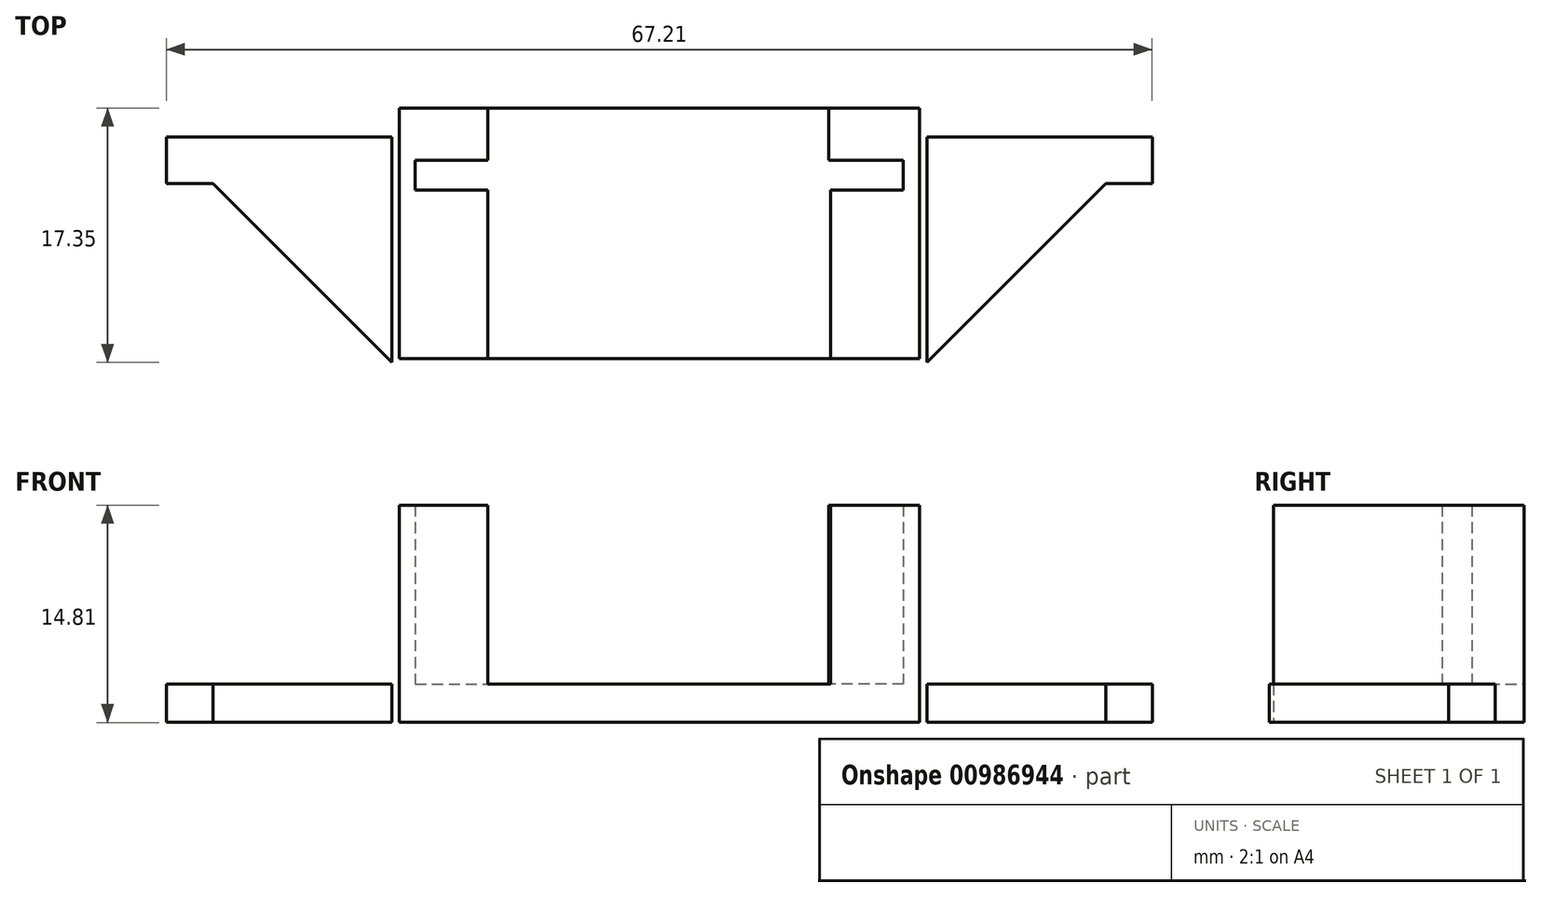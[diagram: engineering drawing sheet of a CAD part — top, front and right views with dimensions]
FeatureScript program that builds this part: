
annotation { "Feature Type Name" : "Feature", "Feature Type Description" : "" }
export const myFeature = defineFeature(function(context is Context, id is Id, definition is map)
    precondition{}
    {
        {
            var Q0;
            Q0=qCreatedBy(makeId("Top.planeOp"),FACE);
            var sketch = newSketch(context, id + "F0", { "sketchPlane" : qUnion([Q0])});
            skLineSegment(sketch, "E0", {"start": v(0, 0) * mm, "end": v(0, -2.03) * mm});
            skLineSegment(sketch, "E1", {"start": v(0, 0) * mm, "end": v(4.57, 0) * mm});
            skLineSegment(sketch, "E2", {"start": v(4.57, 0) * mm, "end": v(4.57, -2.03) * mm});
            skLineSegment(sketch, "E3", {"start": v(0, -2.03) * mm, "end": v(4.57, -2.03) * mm});
            skLineSegment(sketch, "E4.MirrorCS", {"start": v(32.26, -2.03) * mm, "end": v(27.69, -2.03) * mm});
            skLineSegment(sketch, "E5.MirrorCS", {"start": v(32.26, 0) * mm, "end": v(32.26, -2.03) * mm});
            skLineSegment(sketch, "E6.MirrorCS", {"start": v(32.26, 0) * mm, "end": v(27.69, 0) * mm});
            skLineSegment(sketch, "E7.MirrorCS", {"start": v(27.69, 0) * mm, "end": v(27.69, -2.03) * mm});
            skLineSegment(sketch, "E8", {"start": v(-1.6, -1.02) * mm, "end": v(-1.6, 3.56) * mm});
            skLineSegment(sketch, "E9", {"start": v(-1.6, -1.02) * mm, "end": v(-1.6, -5.59) * mm});
            skLineSegment(sketch, "E10", {"start": v(33.86, -1.02) * mm, "end": v(33.86, 3.56) * mm});
            skLineSegment(sketch, "E11", {"start": v(33.86, -1.02) * mm, "end": v(33.86, -5.59) * mm});
            skLineSegment(sketch, "E12.bottom", {"start": v(33.86, -5.59) * mm, "end": v(-1.6, -5.59) * mm});
            skLineSegment(sketch, "E12.top", {"start": v(33.86, 3.56) * mm, "end": v(-1.6, 3.56) * mm});
            skLineSegment(sketch, "E12.left", {"start": v(33.86, -5.59) * mm, "end": v(33.86, 3.56) * mm});
            skLineSegment(sketch, "E12.right", {"start": v(-1.6, -5.59) * mm, "end": v(-1.6, 3.56) * mm});
            skPoint(sketch, "E13.start.orphan", {"position": v(32.26, -1.02) * mm});
            skPoint(sketch, "E14.start.orphan", {"position": v(0, -1.02) * mm});
            skLineSegment(sketch, "E15", {"start": v(4.57, 0) * mm, "end": v(4.57, 3.81) * mm});
            skLineSegment(sketch, "E16", {"start": v(4.57, -2.03) * mm, "end": v(4.57, -9.19) * mm});
            skLineSegment(sketch, "E17", {"start": v(27.69, 0) * mm, "end": v(27.69, 5.45) * mm});
            skLineSegment(sketch, "E18", {"start": v(27.69, 5.45) * mm, "end": v(27.69, -7.68) * mm});
            skSolve(sketch);
        }
        {
            var Q0;
            Q0=makeQuery(id+"F0.imprint","IMPRINT",FACE,{"disambiguationData":[TD([[makeQuery(id+"F0.imprint","IMPRINT",EDGE,{"derivedFrom":sQuery(id+"F0.wireOp",EDGE,"E0")}),-1.0]])]});
            var Q1;
            {var subQ7=sQuery(id+"F0.wireOp",EDGE,"E4.MirrorCS");Q1=makeQuery(id+"F0.imprint","IMPRINT",FACE,{"disambiguationData":[TD([[makeQuery(id+"F0.imprint","IMPRINT",EDGE,{"derivedFrom":subQ7}),1.0]])]});}
            var Q2;
            {var subQ1=sQuery(id+"F0.wireOp",EDGE,"E2");Q2=makeQuery(id+"F0.imprint","IMPRINT",FACE,{"disambiguationData":[TD([[makeQuery(id+"F0.imprint","IMPRINT",EDGE,{"derivedFrom":subQ1}),1.0]])]});}
            var Q3;
            Q3=makeQuery(id+"F0.imprint","IMPRINT",FACE,{"disambiguationData":[TD([[makeQuery(id+"F0.imprint","IMPRINT",EDGE,{"derivedFrom":sQuery(id+"F0.wireOp",EDGE,"E0")}),1.0]])]});
            var Q4;
            {var subQ0=sQuery(id+"F0.wireOp",EDGE,"E4.MirrorCS");Q4=makeQuery(id+"F0.imprint","IMPRINT",FACE,{"disambiguationData":[TD([[makeQuery(id+"F0.imprint","IMPRINT",EDGE,{"derivedFrom":subQ0}),-1.0]])]});}
            extrude(context, id + "F1", {"entities" : qUnion([Q0, Q1, Q2, Q3, Q4]), "depth" : 1.6 * mm, "offsetDistance" : 25.4 * mm});
        }
        {
            var Q0;
            Q0=makeQuery(id+"F1.opExtrude","CAP_FACE",FACE,{"disambiguationData":[OSD([sQuery(id+"F0.wireOp",EDGE,"E12.bottom"),sQuery(id+"F0.wireOp",EDGE,"E12.top"),sQuery(id+"F0.wireOp",EDGE,"E12.left"),sQuery(id+"F0.wireOp",EDGE,"E12.right")])],"isStart":false});
            var sketch = newSketch(context, id + "F2", { "sketchPlane" : qUnion([Q0])});
            skLineSegment(sketch, "E19", {"start": v(0, 0) * mm, "end": v(0, -2.03) * mm});
            skLineSegment(sketch, "E20", {"start": v(0, 0) * mm, "end": v(4.57, 0) * mm});
            skLineSegment(sketch, "E21", {"start": v(4.57, 0) * mm, "end": v(4.57, -2.03) * mm});
            skLineSegment(sketch, "E22", {"start": v(0, -2.03) * mm, "end": v(4.57, -2.03) * mm});
            skLineSegment(sketch, "E23.MirrorCS", {"start": v(32.26, -2.03) * mm, "end": v(27.69, -2.03) * mm});
            skLineSegment(sketch, "E24.MirrorCS", {"start": v(32.26, 0) * mm, "end": v(32.26, -2.03) * mm});
            skLineSegment(sketch, "E25.MirrorCS", {"start": v(32.26, 0) * mm, "end": v(27.69, 0) * mm});
            skLineSegment(sketch, "E26.MirrorCS", {"start": v(27.69, 0) * mm, "end": v(27.69, -2.03) * mm});
            skLineSegment(sketch, "E27", {"start": v(-1.6, -1.02) * mm, "end": v(-1.6, 3.56) * mm});
            skLineSegment(sketch, "E28", {"start": v(-1.6, -1.02) * mm, "end": v(-1.6, -5.59) * mm});
            skLineSegment(sketch, "E29", {"start": v(33.86, -1.02) * mm, "end": v(33.86, 3.56) * mm});
            skLineSegment(sketch, "E30", {"start": v(33.86, -1.02) * mm, "end": v(33.86, -5.59) * mm});
            skLineSegment(sketch, "E31.bottom", {"start": v(33.86, -5.59) * mm, "end": v(-1.6, -5.59) * mm});
            skLineSegment(sketch, "E31.top", {"start": v(33.86, 3.56) * mm, "end": v(-1.6, 3.56) * mm});
            skLineSegment(sketch, "E31.left", {"start": v(33.86, -5.59) * mm, "end": v(33.86, 3.56) * mm});
            skLineSegment(sketch, "E31.right", {"start": v(-1.6, -5.59) * mm, "end": v(-1.6, 3.56) * mm});
            skPoint(sketch, "E32.start.orphan", {"position": v(32.26, -1.02) * mm});
            skPoint(sketch, "E33.start.orphan", {"position": v(0, -1.02) * mm});
            skLineSegment(sketch, "E34", {"start": v(4.57, 0) * mm, "end": v(4.57, 3.81) * mm});
            skLineSegment(sketch, "E35", {"start": v(4.57, -2.03) * mm, "end": v(4.57, -9.19) * mm});
            skLineSegment(sketch, "E36", {"start": v(27.69, 0) * mm, "end": v(27.69, 5.45) * mm});
            skLineSegment(sketch, "E37", {"start": v(27.69, 5.45) * mm, "end": v(27.69, -7.68) * mm});
            skSolve(sketch);
        }
        {
            var Q0;
            Q0=makeQuery(id+"F2.imprint","IMPRINT",FACE,{"disambiguationData":[TD([[makeQuery(id+"F2.imprint","IMPRINT",EDGE,{"derivedFrom":sQuery(id+"F2.wireOp",EDGE,"E19")}),-1.0]])]});
            var Q1;
            {var subQ7=sQuery(id+"F2.wireOp",EDGE,"E23.MirrorCS");Q1=makeQuery(id+"F2.imprint","IMPRINT",FACE,{"disambiguationData":[TD([[makeQuery(id+"F2.imprint","IMPRINT",EDGE,{"derivedFrom":subQ7}),1.0]])]});}
            extrude(context, id + "F3", {"entities" : qUnion([Q0, Q1]), "operationType" : NewBodyOperationType.ADD, "depth" : 12.2 * mm, "offsetDistance" : 25.4 * mm});
        }
        {
            var Q0;
            {var subQ0=sQuery(id+"F2.wireOp",EDGE,"E31.bottom");Q0=makeQuery(id+"F3.boolean.opBoolean","MERGE",FACE,{"derivedFrom":[makeQuery(id+"F1.opExtrude","SWEPT_FACE",FACE,{"disambiguationData":[OSD([sQuery(id+"F0.wireOp",EDGE,"E12.bottom")])]}),makeQuery(id+"F3.opExtrude","SWEPT_FACE",FACE,{"disambiguationData":[OSD([subQ0]),TDD([makeQuery(id+"F2.imprint","IMPRINT",EDGE,{"disambiguationData":[TD([[makeQuery(id+"F2.imprint","INTERSECT",VERTEX,{"derivedFrom":[subQ0,sQuery(id+"F2.wireOp",EDGE,"E31.left")]}),-1.0]])],"derivedFrom":subQ0})])]}),makeQuery(id+"F3.opExtrude","SWEPT_FACE",FACE,{"disambiguationData":[OSD([subQ0]),TDD([makeQuery(id+"F2.imprint","IMPRINT",EDGE,{"disambiguationData":[TD([[makeQuery(id+"F2.imprint","INTERSECT",VERTEX,{"derivedFrom":[subQ0,sQuery(id+"F2.wireOp",EDGE,"E31.right")]}),1.0]])],"derivedFrom":subQ0})])]})]});}
            extrude(context, id + "F4", {"entities" : qUnion([Q0]), "operationType" : NewBodyOperationType.ADD, "depth" : 3.17 * mm, "offsetDistance" : 25.4 * mm});
        }
        {
            var Q0;
            {var subQ0=sQuery(id+"F2.wireOp",EDGE,"E31.right");var subQ1=sQuery(id+"F0.wireOp",EDGE,"E12.right");Q0=makeQuery(id+"F4.boolean.opBoolean","MERGE",FACE,{"derivedFrom":[makeQuery(id+"F3.boolean.opBoolean","MERGE",FACE,{"derivedFrom":[makeQuery(id+"F1.opExtrude","SWEPT_FACE",FACE,{"disambiguationData":[OSD([subQ1])]}),makeQuery(id+"F3.opExtrude","SWEPT_FACE",FACE,{"disambiguationData":[OSD([subQ0])]})]}),makeQuery(id+"F4.opExtrude","SWEPT_FACE",FACE,{"disambiguationData":[OSD([sQuery(id+"F0.wireOp",EDGE,"E12.bottom"),subQ1,sQuery(id+"F2.wireOp",EDGE,"E31.bottom"),subQ0])]})]});}
            extrude(context, id + "F5", {"entities" : qUnion([Q0]), "operationType" : NewBodyOperationType.ADD, "depth" : 0.5 * mm, "offsetDistance" : 25.4 * mm});
        }
        {
            var Q0;
            Q0=makeQuery(id+"F3.opExtrude","SWEPT_FACE",FACE,{"disambiguationData":[OSD([sQuery(id+"F2.wireOp",EDGE,"E19")])]});
            extrude(context, id + "F6", {"entities" : qUnion([Q0]), "operationType" : NewBodyOperationType.REMOVE, "oppositeDirection" : true, "depth" : 0.5 * mm, "offsetDistance" : 25.4 * mm});
        }
        {
            var Q0;
            {var subQ0=sQuery(id+"F2.wireOp",EDGE,"E31.left");var subQ1=sQuery(id+"F0.wireOp",EDGE,"E12.left");Q0=makeQuery(id+"F4.boolean.opBoolean","MERGE",FACE,{"derivedFrom":[makeQuery(id+"F3.boolean.opBoolean","MERGE",FACE,{"derivedFrom":[makeQuery(id+"F1.opExtrude","SWEPT_FACE",FACE,{"disambiguationData":[OSD([subQ1])]}),makeQuery(id+"F3.opExtrude","SWEPT_FACE",FACE,{"disambiguationData":[OSD([subQ0])]})]}),makeQuery(id+"F4.opExtrude","SWEPT_FACE",FACE,{"disambiguationData":[OSD([sQuery(id+"F0.wireOp",EDGE,"E12.bottom"),subQ1,sQuery(id+"F2.wireOp",EDGE,"E31.bottom"),subQ0])]})]});}
            extrude(context, id + "F7", {"entities" : qUnion([Q0]), "operationType" : NewBodyOperationType.ADD, "depth" : 0.5 * mm, "offsetDistance" : 25.4 * mm});
        }
        {
            var Q0;
            Q0=makeQuery(id+"F3.opExtrude","SWEPT_FACE",FACE,{"disambiguationData":[OSD([sQuery(id+"F2.wireOp",EDGE,"E24.MirrorCS")])]});
            extrude(context, id + "F8", {"entities" : qUnion([Q0]), "operationType" : NewBodyOperationType.REMOVE, "oppositeDirection" : true, "depth" : 0.5 * mm, "offsetDistance" : 25.4 * mm});
        }
        {
            var Q0;
            {var subQ0=sQuery(id+"F2.wireOp",EDGE,"E35");Q0=makeQuery(id+"F4.boolean.opBoolean","MERGE",FACE,{"derivedFrom":[makeQuery(id+"F3.opExtrude","SWEPT_FACE",FACE,{"disambiguationData":[OSD([subQ0])]}),makeQuery(id+"F4.opExtrude","SWEPT_FACE",FACE,{"disambiguationData":[OSD([sQuery(id+"F2.wireOp",EDGE,"E31.bottom"),subQ0])]})]});}
            var Q1;
            Q1=makeQuery(id+"F3.opExtrude","SWEPT_FACE",FACE,{"disambiguationData":[OSD([sQuery(id+"F2.wireOp",EDGE,"E34")])]});
            extrude(context, id + "F9", {"entities" : qUnion([Q0, Q1]), "operationType" : NewBodyOperationType.REMOVE, "oppositeDirection" : true, "depth" : 0.13 * mm, "offsetDistance" : 25.4 * mm});
        }
        {
            var Q0;
            {var subQ0=sQuery(id+"F2.wireOp",EDGE,"E37");Q0=makeQuery(id+"F3.opExtrude","SWEPT_FACE",FACE,{"disambiguationData":[OSD([subQ0]),TDD([makeQuery(id+"F2.imprint","IMPRINT",EDGE,{"disambiguationData":[TD([[makeQuery(id+"F2.imprint","INTERSECT",VERTEX,{"derivedFrom":[sQuery(id+"F2.wireOp",EDGE,"E25.MirrorCS"),subQ0]}),1.0]])],"derivedFrom":subQ0})])]});}
            var Q1;
            {var subQ0=sQuery(id+"F2.wireOp",EDGE,"E37");var subQ1=sQuery(id+"F2.wireOp",EDGE,"E31.bottom");Q1=makeQuery(id+"F4.boolean.opBoolean","MERGE",FACE,{"derivedFrom":[makeQuery(id+"F3.opExtrude","SWEPT_FACE",FACE,{"disambiguationData":[OSD([subQ0]),TDD([makeQuery(id+"F2.imprint","IMPRINT",EDGE,{"disambiguationData":[TD([[makeQuery(id+"F2.imprint","INTERSECT",VERTEX,{"derivedFrom":[sQuery(id+"F2.wireOp",EDGE,"E23.MirrorCS"),subQ0]}),-1.0]])],"derivedFrom":subQ0})])]}),makeQuery(id+"F4.opExtrude","SWEPT_FACE",FACE,{"disambiguationData":[OSD([subQ1,subQ0])]})]});}
            extrude(context, id + "F10", {"entities" : qUnion([Q0, Q1]), "operationType" : NewBodyOperationType.REMOVE, "oppositeDirection" : true, "depth" : 0.13 * mm, "offsetDistance" : 25.4 * mm});
        }
        {
            var Q0;
            {var subQ0=sQuery(id+"F0.wireOp",EDGE,"E12.left");var subQ1=sQuery(id+"F0.wireOp",EDGE,"E12.bottom");var subQ2=sQuery(id+"F0.wireOp",EDGE,"E12.right");Q0=makeQuery(id+"F7.boolean.opBoolean","MERGE",FACE,{"derivedFrom":[makeQuery(id+"F5.boolean.opBoolean","MERGE",FACE,{"derivedFrom":[makeQuery(id+"F4.boolean.opBoolean","MERGE",FACE,{"derivedFrom":[makeQuery(id+"F1.opExtrude","CAP_FACE",FACE,{"disambiguationData":[OSD([subQ1,sQuery(id+"F0.wireOp",EDGE,"E12.top"),subQ0,subQ2])],"isStart":true}),makeQuery(id+"F4.opExtrude","SWEPT_FACE",FACE,{"disambiguationData":[OSD([subQ1]),TDD([makeQuery(id+"F1.opExtrude","CAP_EDGE",EDGE,{"disambiguationData":[OSD([subQ1])],"isStart":true})])]})]}),makeQuery(id+"F5.opExtrude","SWEPT_FACE",FACE,{"disambiguationData":[OSD([subQ1,subQ2])]})]}),makeQuery(id+"F7.opExtrude","SWEPT_FACE",FACE,{"disambiguationData":[OSD([subQ1,subQ0])]})]});}
            extrude(context, id + "F11", {"entities" : qUnion([Q0]), "operationType" : NewBodyOperationType.ADD, "depth" : 1.59 * mm, "offsetDistance" : 25.4 * mm});
        }
        {
            var Q0;
            {var subQ0=sQuery(id+"F0.wireOp",EDGE,"E12.right");var subQ1=sQuery(id+"F0.wireOp",EDGE,"E12.left");var subQ2=sQuery(id+"F0.wireOp",EDGE,"E12.bottom");var subQ3=sQuery(id+"F2.wireOp",EDGE,"E31.bottom");Q0=makeQuery(id+"F11.boolean.opBoolean","MERGE",FACE,{"derivedFrom":[makeQuery(id+"F7.boolean.opBoolean","MERGE",FACE,{"derivedFrom":[makeQuery(id+"F5.boolean.opBoolean","MERGE",FACE,{"derivedFrom":[makeQuery(id+"F4.opExtrude","CAP_FACE",FACE,{"disambiguationData":[OSD([subQ2,subQ3])],"isStart":false}),makeQuery(id+"F5.opExtrude","SWEPT_FACE",FACE,{"disambiguationData":[OSD([subQ2,subQ0,subQ3,sQuery(id+"F2.wireOp",EDGE,"E31.right")])]})]}),makeQuery(id+"F7.opExtrude","SWEPT_FACE",FACE,{"disambiguationData":[OSD([subQ2,subQ1,subQ3,sQuery(id+"F2.wireOp",EDGE,"E31.left")])]})]}),makeQuery(id+"F11.opExtrude","SWEPT_FACE",FACE,{"disambiguationData":[OSD([subQ2,subQ1,subQ0])]})]});}
            var sketch = newSketch(context, id + "F12", { "sketchPlane" : qUnion([Q0])});
            skLineSegment(sketch, "E38", {"start": v(-2.1, 13.8) * mm, "end": v(-2.1, -1.59) * mm});
            skLineSegment(sketch, "E39", {"start": v(-2.1, -1.59) * mm, "end": v(-17.48, -1.59) * mm});
            skLineSegment(sketch, "E40", {"start": v(-17.48, -1.59) * mm, "end": v(-2.1, 13.8) * mm});
            skLineSegment(sketch, "E41", {"start": v(34.37, 13.8) * mm, "end": v(34.37, -1.59) * mm});
            skLineSegment(sketch, "E42", {"start": v(34.37, -1.59) * mm, "end": v(49.73, -1.59) * mm});
            skLineSegment(sketch, "E43", {"start": v(49.73, -1.59) * mm, "end": v(34.37, 13.8) * mm});
            skSolve(sketch);
        }
        {
            var Q0;
            Q0 = qSketchRegion(id + "F12", true);
            var Q1;
            {var subQ0=sQuery(id+"F0.wireOp",EDGE,"E12.right");var subQ1=sQuery(id+"F0.wireOp",EDGE,"E12.left");var subQ2=sQuery(id+"F0.wireOp",EDGE,"E12.top");var subQ3=sQuery(id+"F2.wireOp",EDGE,"E31.left");var subQ4=sQuery(id+"F2.wireOp",EDGE,"E31.top");var subQ5=sQuery(id+"F2.wireOp",EDGE,"E31.right");Q1=makeQuery(id+"F11.boolean.opBoolean","MERGE",FACE,{"derivedFrom":[makeQuery(id+"F7.boolean.opBoolean","MERGE",FACE,{"derivedFrom":[makeQuery(id+"F5.boolean.opBoolean","MERGE",FACE,{"derivedFrom":[makeQuery(id+"F3.boolean.opBoolean","MERGE",FACE,{"derivedFrom":[makeQuery(id+"F1.opExtrude","SWEPT_FACE",FACE,{"disambiguationData":[OSD([subQ2])]}),makeQuery(id+"F3.opExtrude","SWEPT_FACE",FACE,{"disambiguationData":[OSD([subQ4]),TDD([makeQuery(id+"F2.imprint","IMPRINT",EDGE,{"disambiguationData":[TD([[makeQuery(id+"F2.imprint","INTERSECT",VERTEX,{"derivedFrom":[subQ4,subQ3]}),-1.0]])],"derivedFrom":subQ4})])]}),makeQuery(id+"F3.opExtrude","SWEPT_FACE",FACE,{"disambiguationData":[OSD([subQ4]),TDD([makeQuery(id+"F2.imprint","IMPRINT",EDGE,{"disambiguationData":[TD([[makeQuery(id+"F2.imprint","INTERSECT",VERTEX,{"derivedFrom":[subQ4,subQ5]}),1.0]])],"derivedFrom":subQ4})])]})]}),makeQuery(id+"F5.opExtrude","SWEPT_FACE",FACE,{"disambiguationData":[OSD([subQ2,subQ0,subQ4,subQ5])]})]}),makeQuery(id+"F7.opExtrude","SWEPT_FACE",FACE,{"disambiguationData":[OSD([subQ2,subQ1,subQ4,subQ3])]})]}),makeQuery(id+"F11.opExtrude","SWEPT_FACE",FACE,{"disambiguationData":[OSD([subQ2,subQ1,subQ0])]})]});}
            extrude(context, id + "F13", {"entities" : qUnion([Q0]), "operationType" : NewBodyOperationType.ADD, "endBound" : BoundingType.UP_TO_SURFACE, "oppositeDirection" : true, "depth" : 25.4 * mm, "endBoundEntityFace" : qUnion([Q1]), "offsetDistance" : 25.4 * mm});
        }
        {
            var Q0;
            Q0=makeQuery(id+"F13.boolean.opBoolean","MERGE",FACE,{"derivedFrom":[makeQuery(id+"F11.opExtrude","CAP_FACE",FACE,{"disambiguationData":[OSD([sQuery(id+"F0.wireOp",EDGE,"E12.bottom"),sQuery(id+"F0.wireOp",EDGE,"E12.top"),sQuery(id+"F0.wireOp",EDGE,"E12.left"),sQuery(id+"F0.wireOp",EDGE,"E12.right")])],"isStart":false}),makeQuery(id+"F13.opExtrude","SWEPT_FACE",FACE,{"disambiguationData":[OSD([sQuery(id+"F12.wireOp",EDGE,"E39")])]}),makeQuery(id+"F13.opExtrude","SWEPT_FACE",FACE,{"disambiguationData":[OSD([sQuery(id+"F12.wireOp",EDGE,"E42")])]})]});
            extrude(context, id + "F14", {"entities" : qUnion([Q0]), "operationType" : NewBodyOperationType.ADD, "depth" : 3.17 * mm, "offsetDistance" : 25.4 * mm});
        }
    });
